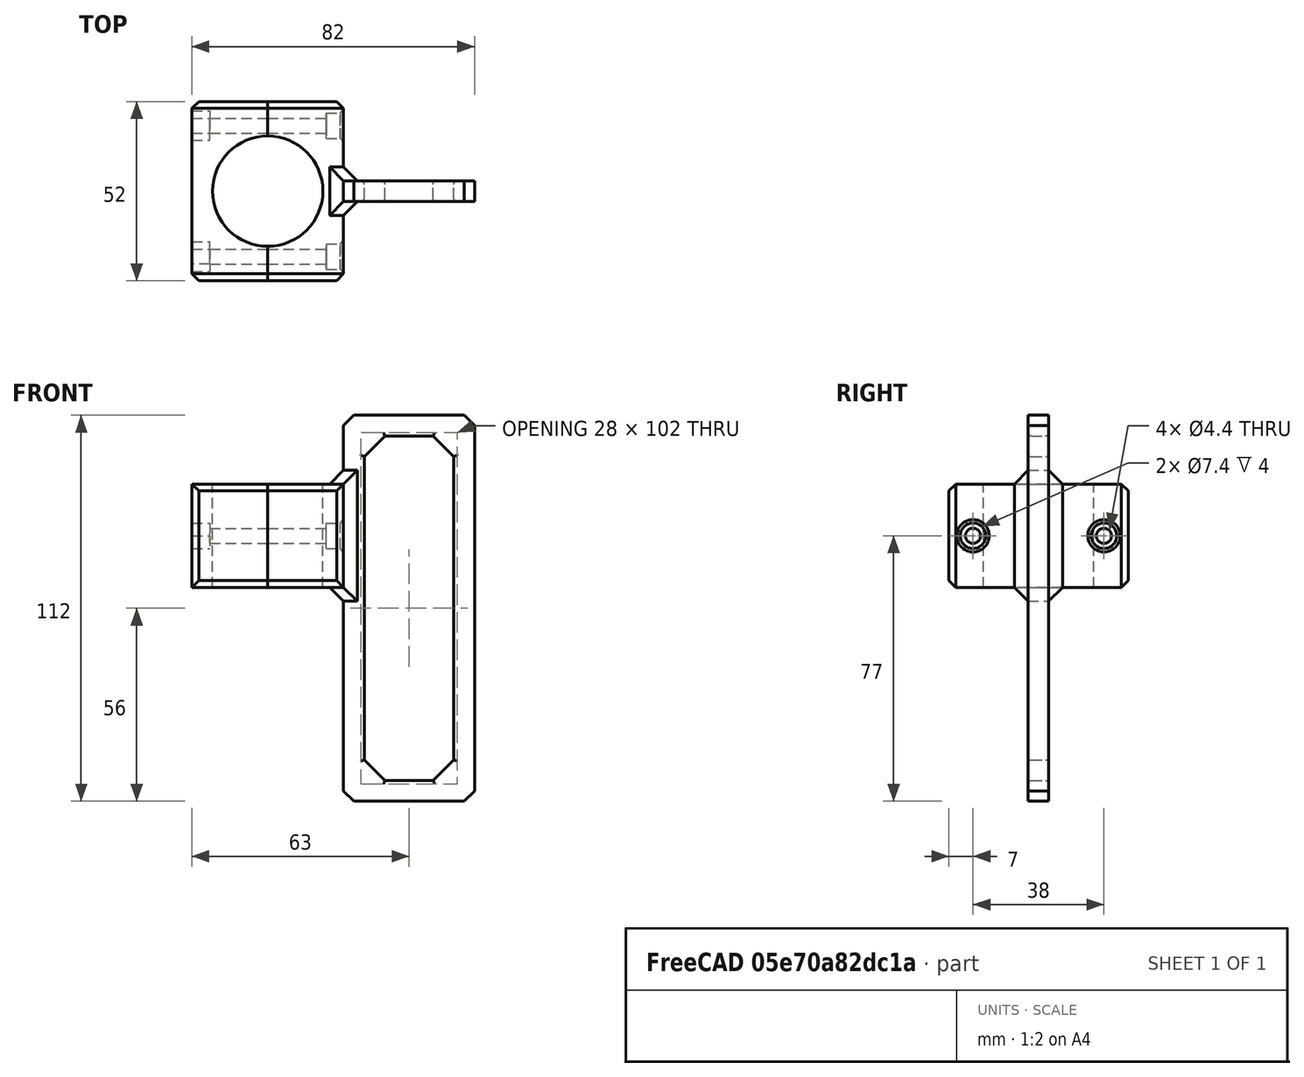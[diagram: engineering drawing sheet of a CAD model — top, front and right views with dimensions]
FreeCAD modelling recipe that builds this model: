
FCSTD DOCUMENT  (FreeCAD 0.19R24276 (Git))
Label: Guia_cable_embrague_SR250_final
License: All rights reserved
LicenseURL: http://en.wikipedia.org/wiki/All_rights_reserved
objects: TechDraw::DrawViewDimension×13, Part::Chamfer×7, Part::Cylinder×6, Part::Cut×6, Part::MultiFuse×6, Part::Mirroring×4, Part::Box×3, Part::Fillet×3, TechDraw::DrawSVGTemplate×2, TechDraw::DrawViewPart×2, TechDraw::DrawProjGroupItem×2, TechDraw::DrawPage×2, Part::Feature×1, Part::Offset×1, TechDraw::DrawProjGroup×1, TechDraw::DrawViewAnnotation×1
note: 37 computed .brp shape members not serialized (recipe doc carries the construction recipe); baked Part::Feature solids carry a one-line shape summary decoded from their .brp

FEATURE [Part::Cylinder] Cylinder  label="barra"
  Angle = 360
  AttacherType = Attacher::AttachEngine3D
  Height = 100
  Radius = 16
FEATURE [Part::Box] Box  label="Cube"
  AttacherType = Attacher::AttachEngine3D
  Height = 30
  Length = 22
  Placement = pos=(0,-26,0) rot=(0,0,1;0rad)
  Width = 52
FEATURE [Part::Box] Box001  label="Cube001"
  AttacherType = Attacher::AttachEngine3D
  Height = 112
  Length = 38
  Placement = pos=(22,-3,-62) rot=(0,0,1;0rad)
  Width = 6
FEATURE [Part::Box] Box002  label="Cube002"
  AttacherType = Attacher::AttachEngine3D
  Height = 100
  Length = 26
  Placement = pos=(28,-3,-56) rot=(0,0,1;0rad)
  Width = 6
FEATURE [Part::Cut] Cut
  Base = -> Box001
  Tool = -> Box002
FEATURE [Part::Chamfer] Chamfer
  Base = -> Cut
  Edges = 4 edges r=3: [Edge2,Edge4,Edge13,Edge20]
FEATURE [Part::Chamfer] Chamfer001
  Base = -> Chamfer
  Edges = 4 edges r=6: [Edge33,Edge34,Edge35,Edge36]
FEATURE [Part::Fillet] Fillet
  Base = -> Chamfer001
  Edges = 4 edges r=1: [Edge1,Edge8,Edge19,Edge32]
FEATURE [Part::Fillet] Fillet001
  Base = -> Fillet
  Edges = 4 edges r=1: [Edge4,Edge9,Edge29,Edge41]
FEATURE [Part::Fillet] Fillet002
  Base = -> Fillet001
  Edges = 8 edges r=1: [Edge2,Edge7,Edge10,Edge15,Edge29,Edge39,Edge50,Edge60]
FEATURE [Part::Chamfer] Chamfer002
  Base = -> Box
  Edges = 6 edges r=2: [Edge5,Edge7,Edge9,Edge10,Edge11,Edge12]
FEATURE [Part::Mirroring] Part__Mirroring004  label="cierre"
  Base = (0,0,0)
  Normal = (1,0,0)
  Source = -> Chamfer002
FEATURE [Part::MultiFuse] Fusion
  Shapes = -> [Chamfer002,Fillet002]
FEATURE [Part::Chamfer] Chamfer003  label="Chamfer005"
  Base = -> Fusion
  Edges = 2 edges r=4: [Edge30,Edge32]
FEATURE [Part::Chamfer] Chamfer004  label="Chamfer006"
  Base = -> Chamfer003
  Edges = 2 edges r=4: [Edge6,Edge102]
FEATURE [Part::Chamfer] Chamfer005  label="Guia"
  Base = -> Chamfer004
  Edges = 8 edges r=4: [Edge1,Edge2,Edge5,Edge7,Edge20,Edge22,Edge61,Edge63]
FEATURE [Part::Cylinder] Cylinder002  label="Cylinder001"
  Angle = 360
  AttacherType = Attacher::AttachEngine3D
  Height = 70
  Placement = pos=(0,0,0) rot=(0,1,0;1.5708rad)
  Radius = 2.2
FEATURE [Part::Cylinder] Cylinder003  label="Cylinder002"
  Angle = 360
  AttacherType = Attacher::AttachEngine3D
  Height = 6
  Placement = pos=(70,0,0) rot=(0,1,0;1.5708rad)
  Radius = 3.7
FEATURE [Part::MultiFuse] Fusion004  label="tornilloM4"
  Placement = pos=(-53,-19,15) rot=(0,0,1;0rad)
  Shapes = -> [Cylinder002,Cylinder003]
FEATURE [Part::Feature] Part__Feature  label="tuercaM4"
  Placement = pos=(-22,-19,15) rot=(0,1,0;1.5708rad)
  shape: bbox 5 x 8.083 x 7 mm, 8 faces (baked)
FEATURE [Part::Cylinder] Cylinder004  label="barra_cp"
  Angle = 360
  AttacherType = Attacher::AttachEngine3D
  Height = 100
  Radius = 16
FEATURE [Part::Cut] Cut001
  Base = -> Chamfer005
  Tool = -> Cylinder
FEATURE [Part::Mirroring] Part__Mirroring  label="tornilloM4 (Mirror #3)"
  Base = (0,0,0)
  Normal = (0,1,0)
  Source = -> Fusion004
FEATURE [Part::MultiFuse] Fusion007  label="tornillos"
  Shapes = -> [Part__Mirroring,Fusion004]
FEATURE [Part::Cylinder] Cylinder005  label="Cylinder003"
  Angle = 360
  AttacherType = Attacher::AttachEngine3D
  Height = 70
  Placement = pos=(0,0,0) rot=(0,1,0;1.5708rad)
  Radius = 2.2
FEATURE [Part::Cylinder] Cylinder006  label="Cylinder005"
  Angle = 360
  AttacherType = Attacher::AttachEngine3D
  Height = 6
  Placement = pos=(70,0,0) rot=(0,1,0;1.5708rad)
  Radius = 3.7
FEATURE [Part::MultiFuse] Fusion008  label="tornilloM005"
  Placement = pos=(-53,-19,15) rot=(0,0,1;0rad)
  Shapes = -> [Cylinder005,Cylinder006]
FEATURE [Part::Mirroring] Part__Mirroring006  label="tornilloM4 (Mirror #3)001"
  Base = (0,0,0)
  Normal = (0,1,0)
  Source = -> Fusion008
FEATURE [Part::MultiFuse] Fusion009  label="tornillos_cp"
  Shapes = -> [Part__Mirroring006,Fusion008]
FEATURE [Part::Cut] Cut002
  Base = -> Cut001
  Tool = -> Fusion007
FEATURE [Part::Chamfer] Chamfer006  label="guia_final"
  Base = -> Cut002
  Edges = 2 edges r=1: [Edge21,Edge44]
FEATURE [Part::Cut] Cut003
  Base = -> Part__Mirroring004
  Tool = -> Cylinder004
FEATURE [Part::Offset] Offset
  Fill = false
  Intersection = false
  Join = 2
  Mode = 0
  SelfIntersection = false
  Source = -> Part__Feature
  Value = 0.2
FEATURE [Part::Mirroring] Part__Mirroring007  label="Offset (Mirror #4)"
  Base = (0,0,0)
  Normal = (0,1,0)
  Source = -> Offset
FEATURE [Part::MultiFuse] Fusion010
  Shapes = -> [Part__Mirroring007,Offset]
FEATURE [Part::Cut] Cut004
  Base = -> Cut003
  Tool = -> Fusion010
FEATURE [Part::Cut] Cut005  label="cierre_final"
  Base = -> Cut004
  Tool = -> Fusion009
FEATURE [TechDraw::DrawSVGTemplate] Template
  EditableTexts = Designed_by_Name=<owner>; Drawing_number=001; FC-Date=-; FC-SC=1:1; FC-SH=1/2; FC-Title=ClutchCableGuide; Subtitle=Guia Cable Embrague; Weight=<250gr
  Height = 210
  Orientation = 1
  Width = 297
FEATURE [TechDraw::DrawSVGTemplate] Template001
  EditableTexts = Designed_by_Name=<owner>; Drawing_number=001; FC-Date=-; FC-SC=1:1; FC-SH=2/2; FC-Title=ClutchCableGuide; Subtitle=Guia Cable Embrague; Weight=<250gr
  Height = 210
  Orientation = 1
  Width = 297
FEATURE [TechDraw::DrawViewPart] View001
  CoarseView = false
  Direction = (0.577,-0.577,0.577)
  Focus = 100
  HardHidden = false
  IsoCount = 0
  IsoHidden = false
  IsoVisible = false
  LockPosition = false
  Perspective = false
  Rotation = 0
  ScaleType = 0
  SeamHidden = false
  SeamVisible = true
  SmoothHidden = false
  SmoothVisible = true
  X = 142.883
  XDirection = (0.707,0.707,0)
  Y = 131.4
FEATURE [TechDraw::DrawViewPart] View
  CoarseView = false
  Direction = (0.577,-0.577,0.577)
  Focus = 100
  HardHidden = false
  IsoCount = 0
  IsoHidden = false
  IsoVisible = false
  LockPosition = false
  Perspective = false
  Rotation = 0
  ScaleType = 2
  SeamHidden = false
  SeamVisible = true
  SmoothHidden = false
  SmoothVisible = true
  X = 222.147
  XDirection = (0.707,0.707,0)
  Y = 125.26
FEATURE [TechDraw::DrawProjGroupItem] ProjItem  label="Front"
  CoarseView = false
  Direction = (0,-1,0)
  Focus = 100
  HardHidden = false
  IsoCount = 0
  IsoHidden = false
  IsoVisible = false
  LockPosition = true
  Perspective = false
  Rotation = 0
  RotationVector = (1,0,0)
  ScaleType = 2
  SeamHidden = false
  SeamVisible = true
  SmoothHidden = false
  SmoothVisible = true
  Type = 0
  X = 0
  XDirection = (1,0,0)
  Y = 0
FEATURE [TechDraw::DrawProjGroupItem] ProjItem002  label="Right"
  CoarseView = false
  Direction = (1,-1e-16,0)
  Focus = 100
  HardHidden = false
  IsoCount = 0
  IsoHidden = false
  IsoVisible = false
  LockPosition = false
  Perspective = false
  Rotation = 0
  RotationVector = (1,0,0)
  ScaleType = 2
  SeamHidden = false
  SeamVisible = true
  SmoothHidden = false
  SmoothVisible = true
  Type = 2
  X = -82
  XDirection = (1e-16,1,0)
  Y = 0
FEATURE [TechDraw::DrawProjGroup] ProjGroup
  Anchor = -> ProjItem
  AutoDistribute = false
  LockPosition = false
  ProjectionType = 0
  Rotation = 0
  ScaleType = 2
  Views = -> [ProjItem,ProjItem002]
  X = 129.571
  Y = 128.977
  spacingX = 15
  spacingY = 15
FEATURE [TechDraw::DrawViewAnnotation] Annotation
  Font = osifont
  LineSpace = 80
  LockPosition = false
  MaxWidth = -1
  Rotation = 0
  ScaleType = 0
  Text = Aproximate measurements: | Check with 3D piece
  TextSize = 5
  TextStyle = 0
  X = 63.7
  Y = 82.6
FEATURE [TechDraw::DrawViewDimension] Dimension
  Arbitrary = false
  ArbitraryTolerances = false
  EqualTolerance = true
  FormatSpec = %.2f
  FormatSpecOverTolerance = %+.2f
  FormatSpecUnderTolerance = %+.2f
  Inverted = false
  LockPosition = false
  MeasureType = 1
  OverTolerance = 0
  References2D = -> [ProjItem002]
  Rotation = 0
  ScaleType = 0
  TheoreticalExact = false
  Type = 2
  UnderTolerance = 0
  X = 26.2
  Y = 1.2
FEATURE [TechDraw::DrawViewDimension] Dimension001
  Arbitrary = false
  ArbitraryTolerances = false
  EqualTolerance = true
  FormatSpec = %.2f
  FormatSpecOverTolerance = %+.2f
  FormatSpecUnderTolerance = %+.2f
  Inverted = false
  LockPosition = false
  MeasureType = 1
  OverTolerance = 0
  References2D = -> [ProjItem]
  Rotation = 0
  ScaleType = 0
  TheoreticalExact = false
  Type = 1
  UnderTolerance = 0
  X = -0.4
  Y = -61.1
FEATURE [TechDraw::DrawPage] Page  label="Vistas"
  KeepUpdated = true
  NextBalloonIndex = 1
  ProjectionType = 0
  Template = -> Template
  Views = -> [View,ProjGroup,Dimension,Dimension001]
FEATURE [TechDraw::DrawViewDimension] Dimension002
  Arbitrary = false
  ArbitraryTolerances = false
  EqualTolerance = true
  FormatSpec = %.2f
  FormatSpecOverTolerance = %+.2f
  FormatSpecUnderTolerance = %+.2f
  Inverted = false
  LockPosition = false
  MeasureType = 1
  OverTolerance = 0
  References2D = -> [View001]
  Rotation = 0
  ScaleType = 0
  TheoreticalExact = false
  Type = 0
  UnderTolerance = 0
  X = -78.5575
  Y = 27.1895
FEATURE [TechDraw::DrawViewDimension] Dimension003
  Arbitrary = false
  ArbitraryTolerances = false
  EqualTolerance = true
  FormatSpec = %.2f
  FormatSpecOverTolerance = %+.2f
  FormatSpecUnderTolerance = %+.2f
  Inverted = false
  LockPosition = false
  MeasureType = 1
  OverTolerance = 0
  References2D = -> [View001]
  Rotation = 0
  ScaleType = 0
  TheoreticalExact = false
  Type = 2
  UnderTolerance = 0
  X = -55.5776
  Y = 15.7896
FEATURE [TechDraw::DrawViewDimension] Dimension004
  Arbitrary = false
  ArbitraryTolerances = false
  EqualTolerance = true
  FormatSpec = %.2f
  FormatSpecOverTolerance = %+.2f
  FormatSpecUnderTolerance = %+.2f
  Inverted = false
  LockPosition = false
  MeasureType = 1
  OverTolerance = 0
  References2D = -> [View001]
  Rotation = 0
  ScaleType = 0
  TheoreticalExact = false
  Type = 0
  UnderTolerance = 0
  X = -29.0668
  Y = -0.266372
FEATURE [TechDraw::DrawViewDimension] Dimension005
  Arbitrary = false
  ArbitraryTolerances = false
  EqualTolerance = true
  FormatSpec = ⌀%.2f
  FormatSpecOverTolerance = %+.2f
  FormatSpecUnderTolerance = %+.2f
  Inverted = false
  LockPosition = false
  MeasureType = 1
  OverTolerance = 0
  References2D = -> [View001]
  Rotation = 0
  ScaleType = 0
  TheoreticalExact = false
  Type = 5
  UnderTolerance = 0
  X = -10.9545
  Y = 44.4264
FEATURE [TechDraw::DrawViewDimension] Dimension006
  Arbitrary = false
  ArbitraryTolerances = false
  EqualTolerance = true
  FormatSpec = %.2f
  FormatSpecOverTolerance = %+.2f
  FormatSpecUnderTolerance = %+.2f
  Inverted = false
  LockPosition = false
  MeasureType = 1
  OverTolerance = 0
  References2D = -> [View001]
  Rotation = 0
  ScaleType = 0
  TheoreticalExact = false
  Type = 0
  UnderTolerance = 0
  X = -22.0453
  Y = -32.87
FEATURE [TechDraw::DrawViewDimension] Dimension007
  Arbitrary = false
  ArbitraryTolerances = false
  EqualTolerance = true
  FormatSpec = %.2f
  FormatSpecOverTolerance = %+.2f
  FormatSpecUnderTolerance = %+.2f
  Inverted = false
  LockPosition = false
  MeasureType = 1
  OverTolerance = 0
  References2D = -> [View001]
  Rotation = 0
  ScaleType = 0
  TheoreticalExact = false
  Type = 2
  UnderTolerance = 0
  X = 60.1681
  Y = -15.6022
FEATURE [TechDraw::DrawViewDimension] Dimension008
  Arbitrary = false
  ArbitraryTolerances = false
  EqualTolerance = true
  FormatSpec = %.2f
  FormatSpecOverTolerance = %+.2f
  FormatSpecUnderTolerance = %+.2f
  Inverted = false
  LockPosition = false
  MeasureType = 1
  OverTolerance = 0
  References2D = -> [View001]
  Rotation = 0
  ScaleType = 0
  TheoreticalExact = false
  Type = 0
  UnderTolerance = 0
  X = 48.292
  Y = 55.3853
FEATURE [TechDraw::DrawViewDimension] Dimension009
  Arbitrary = false
  ArbitraryTolerances = false
  EqualTolerance = true
  FormatSpec = ⌀%.2f
  FormatSpecOverTolerance = %+.2f
  FormatSpecUnderTolerance = %+.2f
  Inverted = false
  LockPosition = false
  MeasureType = 1
  OverTolerance = 0
  References2D = -> [View001]
  Rotation = 0
  ScaleType = 0
  TheoreticalExact = false
  Type = 5
  UnderTolerance = 0
  X = -2.78933
  Y = 0.760726
FEATURE [TechDraw::DrawViewDimension] Dimension010
  Arbitrary = false
  ArbitraryTolerances = false
  EqualTolerance = true
  FormatSpec = %.2f
  FormatSpecOverTolerance = %+.2f
  FormatSpecUnderTolerance = %+.2f
  Inverted = false
  LockPosition = false
  MeasureType = 1
  OverTolerance = 0
  References2D = -> [View001]
  Rotation = 0
  ScaleType = 0
  TheoreticalExact = false
  Type = 0
  UnderTolerance = 0
  X = -9.52207
  Y = -21.3171
FEATURE [TechDraw::DrawViewDimension] Dimension011
  Arbitrary = false
  ArbitraryTolerances = false
  EqualTolerance = true
  FormatSpec = %.2f
  FormatSpecOverTolerance = %+.2f
  FormatSpecUnderTolerance = %+.2f
  Inverted = false
  LockPosition = false
  MeasureType = 1
  OverTolerance = 0
  References2D = -> [View001]
  Rotation = 0
  ScaleType = 0
  TheoreticalExact = false
  Type = 0
  UnderTolerance = 0
  X = -93.6299
  Y = 38.6615
FEATURE [TechDraw::DrawViewDimension] Dimension012
  Arbitrary = false
  ArbitraryTolerances = false
  EqualTolerance = true
  FormatSpec = %.2f
  FormatSpecOverTolerance = %+.2f
  FormatSpecUnderTolerance = %+.2f
  Inverted = false
  LockPosition = false
  MeasureType = 1
  OverTolerance = 0
  References2D = -> [View001]
  Rotation = 0
  ScaleType = 0
  TheoreticalExact = false
  Type = 2
  UnderTolerance = 0
  X = 45.6784
  Y = -8.26445
FEATURE [TechDraw::DrawPage] Page001  label="Cotas"
  KeepUpdated = true
  NextBalloonIndex = 1
  ProjectionType = 0
  Template = -> Template001
  Views = -> [View001,Annotation,Dimension002,Dimension003,Dimension004,Dimension005,Dimension006,Dimension007,Dimension008,Dimension009,Dimension010,Dimension011,Dimension012]
